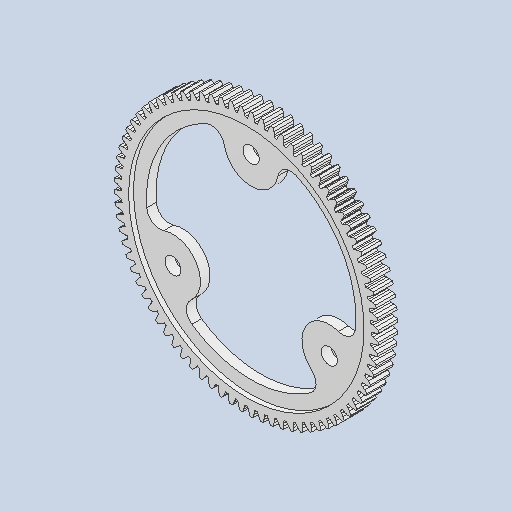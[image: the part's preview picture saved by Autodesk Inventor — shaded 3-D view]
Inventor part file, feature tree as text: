
AUTODESK INVENTOR PART (.ipt)
format: ipt  version: 2023 (Build 270158030, 158C)  size: 1,183,744 bytes
history: native  units: mm
features: extrude x5, sketch x5
ambient origin geometry x8: Origin, YZ Plane, XZ Plane, XY Plane, X Axis, Y Axis, Z Axis, Center Point
bodies: Solid1 (feature_tree)
feature tree (10):
  extrude  "Extrusion1"  Depth=3.0mm
  extrude  "Extrusion2"  Depth=14.0mm
  extrude  "Extrusion3"  Depth=36.5mm
  extrude  "Extrusion4"  Depth=0.75mm TaperAngle=0.0deg
  extrude  "Extrusion5"  Depth=2.0mm TaperAngle=360.0deg
  sketch  "Sketch1"  dims[d0=3.0mm d1=0.0mm d3=2.5mm]
  sketch  "Sketch2"  dims[d4=30.0mm d6=360.0deg d8=14.0mm]
  sketch  "Sketch3"  dims[d9=0.0mm d10=0.0mm d11=36.5mm]
  sketch  "Sketch4"  dims[d12=0.75mm d13=0.0mm d14=0.75mm d15=0.0mm]
  sketch  "Sketch5"  dims[d16=3.0mm d17=30.0mm d19=360.0deg d21=2.0mm d22=2.0mm d23=30.0mm d25=360.0deg d27=0.0mm d28=0.0mm]
